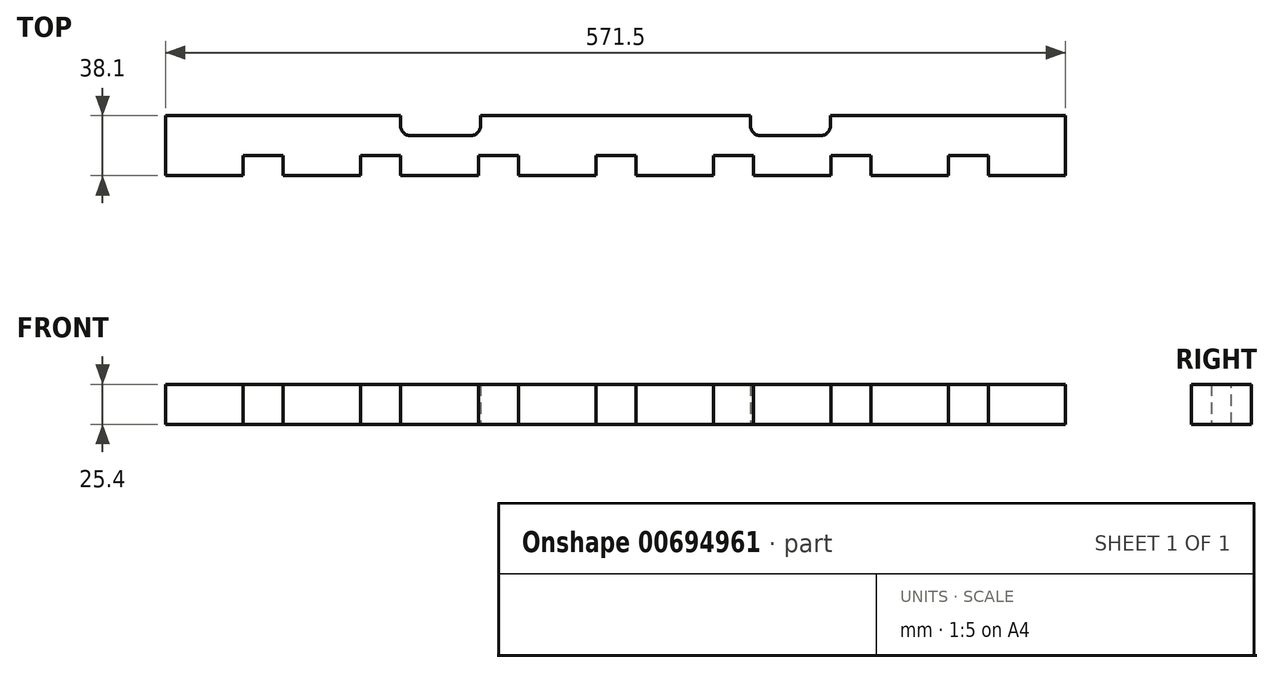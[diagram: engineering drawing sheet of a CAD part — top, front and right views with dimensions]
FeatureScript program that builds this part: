
annotation { "Feature Type Name" : "Feature", "Feature Type Description" : "" }
export const myFeature = defineFeature(function(context is Context, id is Id, definition is map)
    precondition{}
    {
        {
            var Q0;
            Q0=qCreatedBy(makeId("Top.planeOp"),FACE);
            var sketch = newSketch(context, id + "F0", { "sketchPlane" : qUnion([Q0])});
            skLineSegment(sketch, "E0.bottom", {"start": v(-285.75, 19.05) * mm, "end": v(285.75, 19.05) * mm});
            skLineSegment(sketch, "E0.top", {"start": v(-285.75, -19.05) * mm, "end": v(-223.77, -19.05) * mm});
            skLineSegment(sketch, "E0.left", {"start": v(-285.75, 19.05) * mm, "end": v(-285.75, -19.05) * mm});
            skLineSegment(sketch, "E0.right", {"start": v(285.75, 19.05) * mm, "end": v(285.75, -19.05) * mm});
            skPoint(sketch, "E0.middle", {"position": v(0, 0) * mm});
            skLineSegment(sketch, "E1.bottom", {"start": v(-236.47, -6.35) * mm, "end": v(-211.07, -6.35) * mm});
            skLineSegment(sketch, "E1.left", {"start": v(-236.47, -6.35) * mm, "end": v(-236.47, -31.75) * mm});
            skLineSegment(sketch, "E1.right", {"start": v(-211.07, -6.35) * mm, "end": v(-211.07, -31.75) * mm});
            skPoint(sketch, "E1.middle", {"position": v(-223.77, -19.05) * mm});
            skPoint(sketch, "E2.1.0.0", {"position": v(-149.1, -19.05) * mm});
            skLineSegment(sketch, "E2.1.0.1", {"start": v(-161.8, -6.35) * mm, "end": v(-136.4, -6.35) * mm});
            skLineSegment(sketch, "E2.1.0.2", {"start": v(-161.8, -6.35) * mm, "end": v(-161.8, -31.75) * mm});
            skLineSegment(sketch, "E2.1.0.3", {"start": v(-136.4, -6.35) * mm, "end": v(-136.4, -31.75) * mm});
            skPoint(sketch, "E2.2.0.0", {"position": v(-74.42, -19.05) * mm});
            skLineSegment(sketch, "E2.2.0.1", {"start": v(-87.12, -6.35) * mm, "end": v(-61.72, -6.35) * mm});
            skLineSegment(sketch, "E2.2.0.2", {"start": v(-87.12, -6.35) * mm, "end": v(-87.12, -31.75) * mm});
            skLineSegment(sketch, "E2.2.0.3", {"start": v(-61.72, -6.35) * mm, "end": v(-61.72, -31.75) * mm});
            skPoint(sketch, "E2.3.0.0", {"position": v(0.25, -19.05) * mm});
            skLineSegment(sketch, "E2.3.0.1", {"start": v(-12.45, -6.35) * mm, "end": v(12.95, -6.35) * mm});
            skLineSegment(sketch, "E2.3.0.2", {"start": v(-12.45, -6.35) * mm, "end": v(-12.45, -31.75) * mm});
            skLineSegment(sketch, "E2.3.0.3", {"start": v(12.95, -6.35) * mm, "end": v(12.95, -31.75) * mm});
            skPoint(sketch, "E2.4.0.0", {"position": v(74.93, -19.05) * mm});
            skLineSegment(sketch, "E2.4.0.1", {"start": v(62.23, -6.35) * mm, "end": v(87.63, -6.35) * mm});
            skLineSegment(sketch, "E2.4.0.2", {"start": v(62.23, -6.35) * mm, "end": v(62.23, -31.75) * mm});
            skLineSegment(sketch, "E2.4.0.3", {"start": v(87.63, -6.35) * mm, "end": v(87.63, -31.75) * mm});
            skPoint(sketch, "E2.5.0.0", {"position": v(149.6, -19.05) * mm});
            skLineSegment(sketch, "E2.5.0.1", {"start": v(136.9, -6.35) * mm, "end": v(162.3, -6.35) * mm});
            skLineSegment(sketch, "E2.5.0.2", {"start": v(136.9, -6.35) * mm, "end": v(136.9, -31.75) * mm});
            skLineSegment(sketch, "E2.5.0.3", {"start": v(162.3, -6.35) * mm, "end": v(162.3, -31.75) * mm});
            skPoint(sketch, "E2.6.0.0", {"position": v(224.28, -19.05) * mm});
            skLineSegment(sketch, "E2.6.0.1", {"start": v(211.58, -6.35) * mm, "end": v(236.98, -6.35) * mm});
            skLineSegment(sketch, "E2.6.0.2", {"start": v(211.58, -6.35) * mm, "end": v(211.58, -31.75) * mm});
            skLineSegment(sketch, "E2.6.0.3", {"start": v(236.98, -6.35) * mm, "end": v(236.98, -31.75) * mm});
            skLineSegment(sketch, "E2.direction1", {"start": v(-211.07, -31.75) * mm, "end": v(-161.8, -31.75) * mm, "construction": true});
            skLineSegment(sketch, "E3.trimOffspring", {"start": v(-211.07, -19.05) * mm, "end": v(-149.1, -19.05) * mm});
            skLineSegment(sketch, "E4.trimOffspring", {"start": v(-136.4, -19.05) * mm, "end": v(-74.42, -19.05) * mm});
            skLineSegment(sketch, "E5.trimOffspring", {"start": v(-61.72, -19.05) * mm, "end": v(0.25, -19.05) * mm});
            skLineSegment(sketch, "E6.trimOffspring", {"start": v(12.95, -19.05) * mm, "end": v(74.93, -19.05) * mm});
            skLineSegment(sketch, "E7.trimOffspring", {"start": v(87.63, -19.05) * mm, "end": v(149.6, -19.05) * mm});
            skLineSegment(sketch, "E8.trimOffspring", {"start": v(162.3, -19.05) * mm, "end": v(224.28, -19.05) * mm});
            skLineSegment(sketch, "E9.trimOffspring", {"start": v(236.98, -19.05) * mm, "end": v(285.75, -19.05) * mm});
            skSolve(sketch);
        }
        {
            var Q0;
            Q0 = qSketchRegion(id + "F0", true);
            extrude(context, id + "F1", {"entities" : qUnion([Q0]), "depth" : 25.4 * mm, "offsetDistance" : 25.4 * mm});
        }
        {
            var Q0;
            Q0=makeQuery(id+"F1.opExtrude","CAP_FACE",FACE,{"disambiguationData":[OSD([sQuery(id+"F0.wireOp",EDGE,"E0.bottom"),sQuery(id+"F0.wireOp",EDGE,"E0.top"),sQuery(id+"F0.wireOp",EDGE,"E0.left"),sQuery(id+"F0.wireOp",EDGE,"E0.right"),sQuery(id+"F0.wireOp",EDGE,"E1.bottom"),sQuery(id+"F0.wireOp",EDGE,"E1.left"),sQuery(id+"F0.wireOp",EDGE,"E1.right"),sQuery(id+"F0.wireOp",EDGE,"E2.1.0.1"),sQuery(id+"F0.wireOp",EDGE,"E2.1.0.2"),sQuery(id+"F0.wireOp",EDGE,"E2.1.0.3"),sQuery(id+"F0.wireOp",EDGE,"E2.2.0.1"),sQuery(id+"F0.wireOp",EDGE,"E2.2.0.2"),sQuery(id+"F0.wireOp",EDGE,"E2.2.0.3"),sQuery(id+"F0.wireOp",EDGE,"E2.3.0.1"),sQuery(id+"F0.wireOp",EDGE,"E2.3.0.2"),sQuery(id+"F0.wireOp",EDGE,"E2.3.0.3"),sQuery(id+"F0.wireOp",EDGE,"E2.4.0.1"),sQuery(id+"F0.wireOp",EDGE,"E2.4.0.2"),sQuery(id+"F0.wireOp",EDGE,"E2.4.0.3"),sQuery(id+"F0.wireOp",EDGE,"E2.5.0.1"),sQuery(id+"F0.wireOp",EDGE,"E2.5.0.2"),sQuery(id+"F0.wireOp",EDGE,"E2.5.0.3"),sQuery(id+"F0.wireOp",EDGE,"E2.6.0.1"),sQuery(id+"F0.wireOp",EDGE,"E2.6.0.2"),sQuery(id+"F0.wireOp",EDGE,"E2.6.0.3"),sQuery(id+"F0.wireOp",EDGE,"E3.trimOffspring"),sQuery(id+"F0.wireOp",EDGE,"E4.trimOffspring"),sQuery(id+"F0.wireOp",EDGE,"E5.trimOffspring"),sQuery(id+"F0.wireOp",EDGE,"E6.trimOffspring"),sQuery(id+"F0.wireOp",EDGE,"E7.trimOffspring"),sQuery(id+"F0.wireOp",EDGE,"E8.trimOffspring"),sQuery(id+"F0.wireOp",EDGE,"E9.trimOffspring")])],"isStart":false});
            var sketch = newSketch(context, id + "F2", { "sketchPlane" : qUnion([Q0])});
            skLineSegment(sketch, "E10", {"start": v(0, 128.3) * mm, "end": v(0, -125.9) * mm, "construction": true});
            skLineSegment(sketch, "E11.0", {"start": v(-111.13, 128.3) * mm, "end": v(-111.12, -125.9) * mm, "construction": true});
            skLineSegment(sketch, "E12.0", {"start": v(-285.75, 19.05) * mm, "end": v(285.75, 19.05) * mm, "construction": true});
            skLineSegment(sketch, "E13.bottom", {"start": v(-136.53, 6.35) * mm, "end": v(-85.73, 6.35) * mm});
            skLineSegment(sketch, "E13.top", {"start": v(-136.53, 31.75) * mm, "end": v(-85.73, 31.75) * mm});
            skLineSegment(sketch, "E13.left", {"start": v(-136.53, 6.35) * mm, "end": v(-136.53, 31.75) * mm});
            skLineSegment(sketch, "E13.right", {"start": v(-85.73, 6.35) * mm, "end": v(-85.73, 31.75) * mm});
            skPoint(sketch, "E13.middle", {"position": v(-111.12, 19.05) * mm});
            skLineSegment(sketch, "E14.MirrorCS", {"start": v(85.73, 6.35) * mm, "end": v(85.73, 31.75) * mm});
            skLineSegment(sketch, "E15.MirrorCS", {"start": v(136.53, 6.35) * mm, "end": v(136.53, 31.75) * mm});
            skLineSegment(sketch, "E16.MirrorCS", {"start": v(136.53, 31.75) * mm, "end": v(85.73, 31.75) * mm});
            skLineSegment(sketch, "E17.MirrorCS", {"start": v(136.53, 6.35) * mm, "end": v(85.73, 6.35) * mm});
            skPoint(sketch, "E18.MirrorP", {"position": v(111.12, 19.05) * mm});
            skSolve(sketch);
        }
        {
            var Q0;
            Q0 = qSketchRegion(id + "F2", true);
            extrude(context, id + "F3", {"entities" : qUnion([Q0]), "operationType" : NewBodyOperationType.REMOVE, "endBound" : BoundingType.THROUGH_ALL, "oppositeDirection" : true, "depth" : 25.4 * mm, "offsetDistance" : 25.4 * mm});
        }
        {
            var Q0;
            Q0=makeQuery(id+"F3.boolean.opBoolean","COPY",EDGE,{"derivedFrom":makeQuery(id+"F3.opExtrude","SWEPT_EDGE",EDGE,{"disambiguationData":[OSD([sQuery(id+"F2.wireOp",EDGE,"E13.bottom"),sQuery(id+"F2.wireOp",EDGE,"E13.left")])]})});
            var Q1;
            Q1=makeQuery(id+"F3.boolean.opBoolean","COPY",EDGE,{"derivedFrom":makeQuery(id+"F3.opExtrude","SWEPT_EDGE",EDGE,{"disambiguationData":[OSD([sQuery(id+"F2.wireOp",EDGE,"E13.bottom"),sQuery(id+"F2.wireOp",EDGE,"E13.right")])]})});
            var Q2;
            Q2=makeQuery(id+"F3.boolean.opBoolean","COPY",EDGE,{"derivedFrom":makeQuery(id+"F3.opExtrude","SWEPT_EDGE",EDGE,{"disambiguationData":[OSD([sQuery(id+"F2.wireOp",EDGE,"E15.MirrorCS"),sQuery(id+"F2.wireOp",EDGE,"E17.MirrorCS")])]})});
            var Q3;
            Q3=makeQuery(id+"F3.boolean.opBoolean","COPY",EDGE,{"derivedFrom":makeQuery(id+"F3.opExtrude","SWEPT_EDGE",EDGE,{"disambiguationData":[OSD([sQuery(id+"F2.wireOp",EDGE,"E14.MirrorCS"),sQuery(id+"F2.wireOp",EDGE,"E17.MirrorCS")])]})});
            fillet(context, id + "F4", {"entities" : qUnion([Q0, Q1, Q2, Q3]), "radius" : 6.35 * mm, "tangentPropagation" : true, "allowEdgeOverflow" : false});
        }
    });
